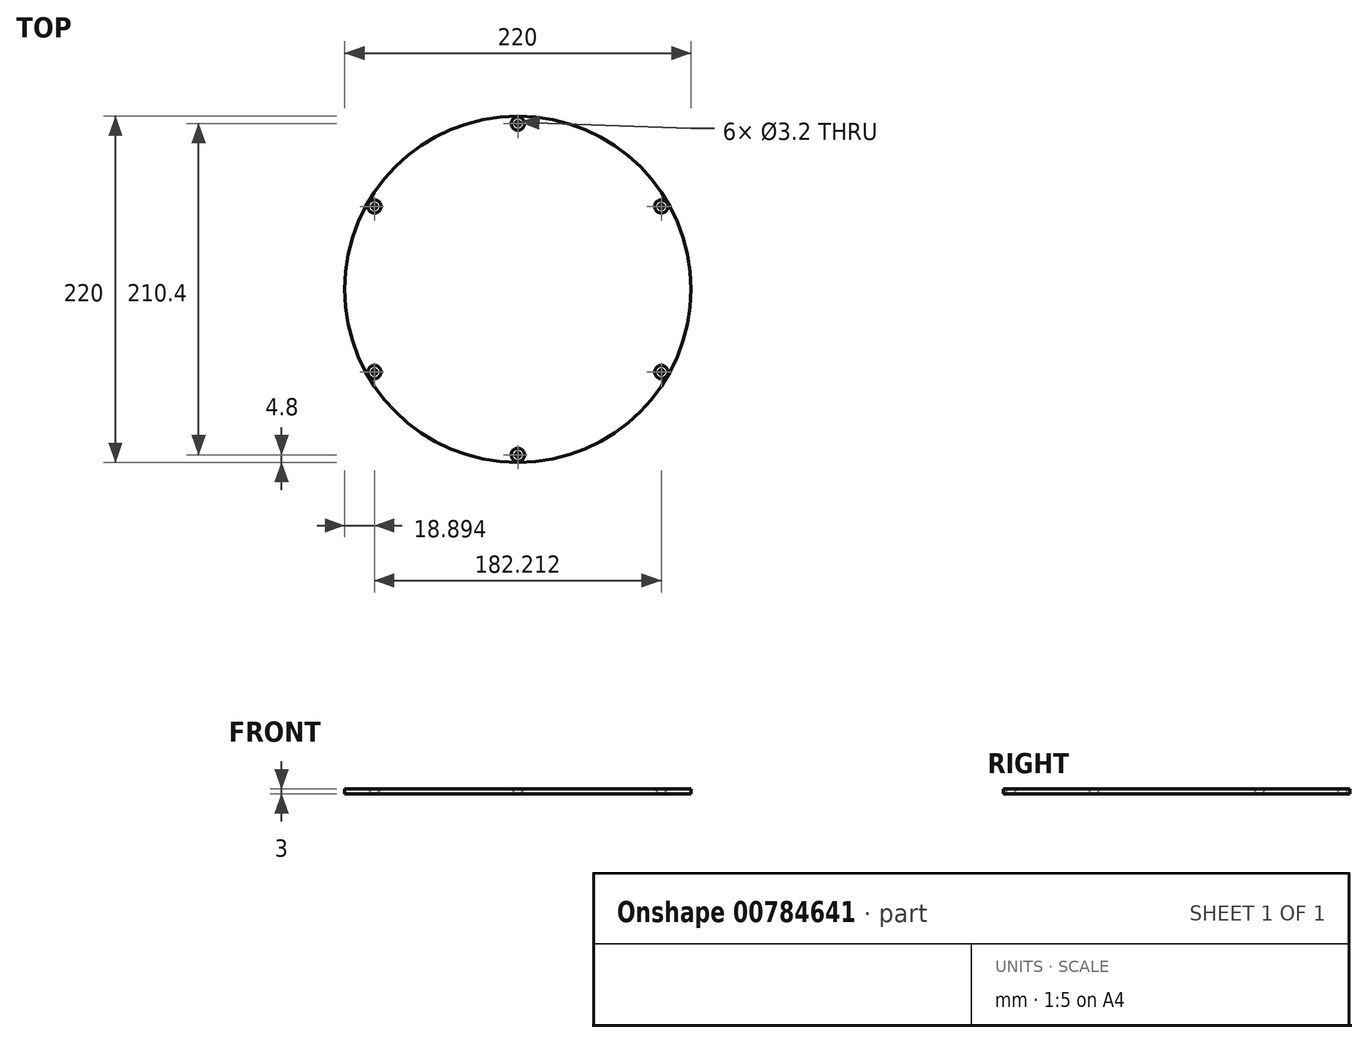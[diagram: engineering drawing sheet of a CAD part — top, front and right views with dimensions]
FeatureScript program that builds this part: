
annotation { "Feature Type Name" : "Feature", "Feature Type Description" : "" }
export const myFeature = defineFeature(function(context is Context, id is Id, definition is map)
    precondition{}
    {
        {
            var Q0;
            Q0=qCreatedBy(makeId("Top.planeOp"),FACE);
            var sketch = newSketch(context, id + "F0", { "sketchPlane" : qUnion([Q0])});
            skCircle(sketch, "E0", {"center": v(0, 0) * mm, "radius": 110 * mm});
            skCircle(sketch, "E1", {"center": v(0, 0) * mm, "radius": 105.2 * mm, "construction": true});
            skCircle(sketch, "E2", {"center": v(0, 105.2) * mm, "radius": 1.6 * mm});
            skCircle(sketch, "E3.1.0", {"center": v(-91.1, 52.6) * mm, "radius": 1.6 * mm});
            skCircle(sketch, "E3.2.0", {"center": v(-91.1, -52.6) * mm, "radius": 1.6 * mm});
            skCircle(sketch, "E3.3.0", {"center": v(0, -105.2) * mm, "radius": 1.6 * mm});
            skCircle(sketch, "E3.4.0", {"center": v(91.1, -52.6) * mm, "radius": 1.6 * mm});
            skCircle(sketch, "E3.5.0", {"center": v(91.1, 52.6) * mm, "radius": 1.6 * mm});
            skSolve(sketch);
        }
        {
            var Q0;
            Q0 = qSketchRegion(id + "F0", true);
            extrude(context, id + "F1", {"entities" : qUnion([Q0]), "depth" : 3 * mm, "offsetDistance" : 25 * mm});
        }
        {
            var Q0;
            Q0=makeQuery(id+"F1.opExtrude","CAP_EDGE",EDGE,{"disambiguationData":[OSD([sQuery(id+"F0.wireOp",EDGE,"E3.1.0")])],"isStart":false});
            var Q1;
            Q1=makeQuery(id+"F1.opExtrude","CAP_EDGE",EDGE,{"disambiguationData":[OSD([sQuery(id+"F0.wireOp",EDGE,"E2")])],"isStart":false});
            var Q2;
            Q2=makeQuery(id+"F1.opExtrude","CAP_EDGE",EDGE,{"disambiguationData":[OSD([sQuery(id+"F0.wireOp",EDGE,"E3.5.0")])],"isStart":false});
            var Q3;
            Q3=makeQuery(id+"F1.opExtrude","CAP_EDGE",EDGE,{"disambiguationData":[OSD([sQuery(id+"F0.wireOp",EDGE,"E3.4.0")])],"isStart":false});
            var Q4;
            Q4=makeQuery(id+"F1.opExtrude","CAP_EDGE",EDGE,{"disambiguationData":[OSD([sQuery(id+"F0.wireOp",EDGE,"E3.3.0")])],"isStart":false});
            var Q5;
            Q5=makeQuery(id+"F1.opExtrude","CAP_EDGE",EDGE,{"disambiguationData":[OSD([sQuery(id+"F0.wireOp",EDGE,"E3.2.0")])],"isStart":false});
            chamfer(context, id + "F2", {"entities" : qUnion([Q0, Q1, Q2, Q3, Q4, Q5]), "width" : 2.6 * mm, "tangentPropagation" : true});
        }
    });
